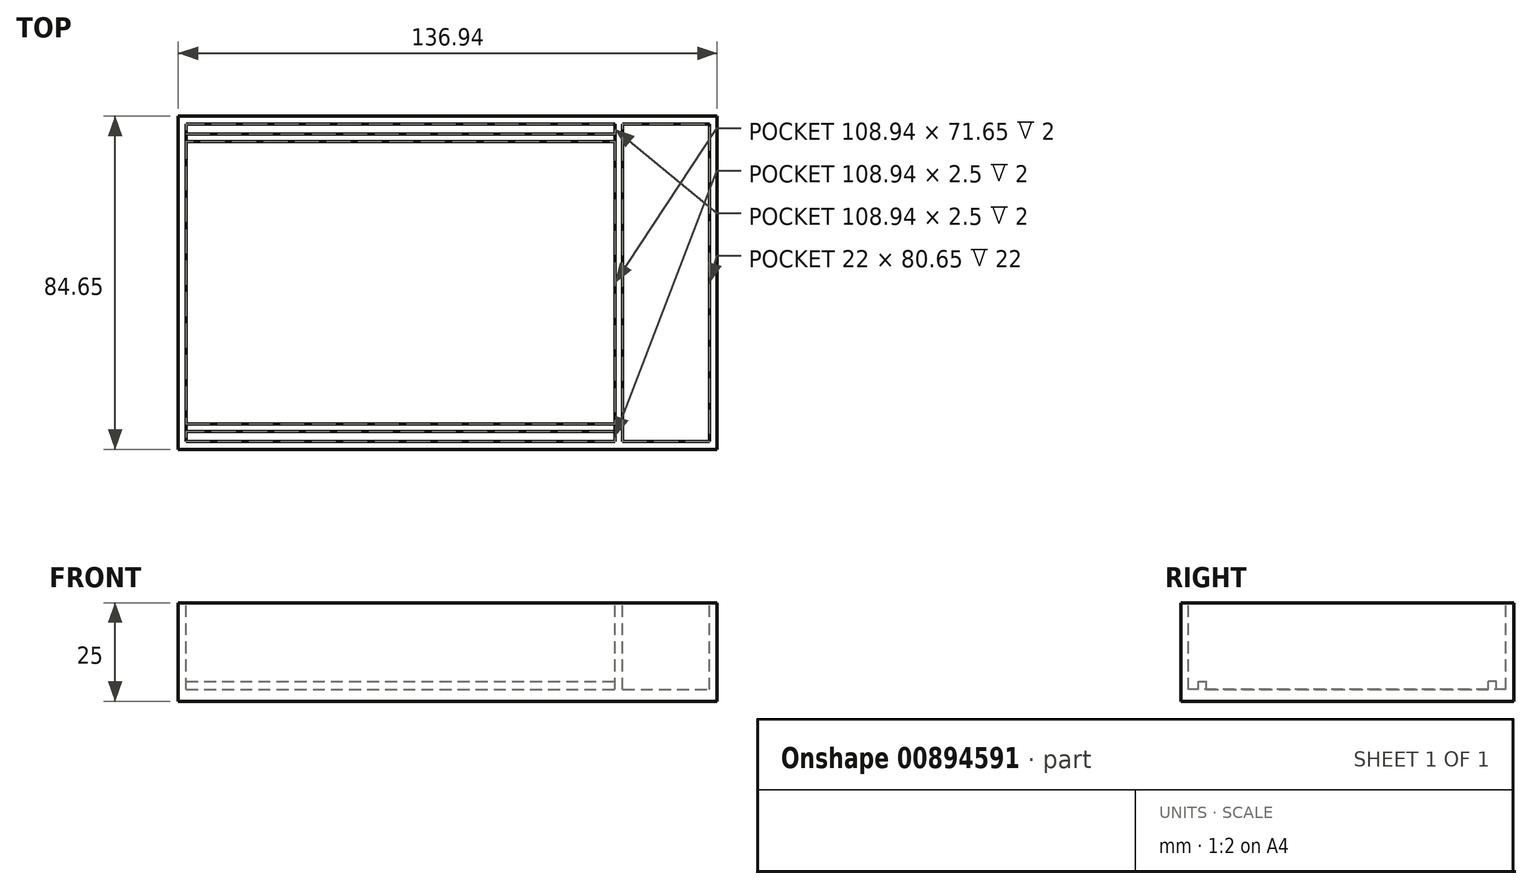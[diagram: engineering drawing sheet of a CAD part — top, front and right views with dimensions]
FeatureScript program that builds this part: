
annotation { "Feature Type Name" : "Feature", "Feature Type Description" : "" }
export const myFeature = defineFeature(function(context is Context, id is Id, definition is map)
    precondition{}
    {
        {
            var Q0;
            Q0=qCreatedBy(makeId("Top.planeOp"),FACE);
            var sketch = newSketch(context, id + "F0", { "sketchPlane" : qUnion([Q0])});
            skLineSegment(sketch, "E0.bottom", {"start": v(0, 0) * mm, "end": v(136.94, 0) * mm});
            skLineSegment(sketch, "E0.top", {"start": v(0, 84.65) * mm, "end": v(136.94, 84.65) * mm});
            skLineSegment(sketch, "E0.left", {"start": v(0, 0) * mm, "end": v(0, 84.65) * mm});
            skLineSegment(sketch, "E0.right", {"start": v(136.94, 0) * mm, "end": v(136.94, 84.65) * mm});
            skSolve(sketch);
        }
        {
            var Q0;
            Q0=makeQuery(id+"F0.imprint","IMPRINT",FACE,{"disambiguationData":[TD([[makeQuery(id+"F0.imprint","IMPRINT",EDGE,{"derivedFrom":sQuery(id+"F0.wireOp",EDGE,"E0.bottom")}),1.0]])]});
            extrude(context, id + "F1", {"entities" : qUnion([Q0]), "depth" : 25 * mm, "offsetDistance" : 25 * mm});
        }
        {
            var Q0;
            Q0=makeQuery(id+"F1.opExtrude","CAP_FACE",FACE,{"disambiguationData":[OSD([sQuery(id+"F0.wireOp",EDGE,"E0.bottom"),sQuery(id+"F0.wireOp",EDGE,"E0.top"),sQuery(id+"F0.wireOp",EDGE,"E0.left"),sQuery(id+"F0.wireOp",EDGE,"E0.right")])],"isStart":false});
            var sketch = newSketch(context, id + "F2", { "sketchPlane" : qUnion([Q0])});
            skLineSegment(sketch, "E1.bottom", {"start": v(2, 6.5) * mm, "end": v(110.94, 6.5) * mm});
            skLineSegment(sketch, "E1.top", {"start": v(2, 78.15) * mm, "end": v(110.94, 78.15) * mm});
            skLineSegment(sketch, "E1.left", {"start": v(2, 6.5) * mm, "end": v(2, 78.15) * mm});
            skLineSegment(sketch, "E1.right", {"start": v(110.94, 6.5) * mm, "end": v(110.94, 78.15) * mm});
            skLineSegment(sketch, "E2.bottom", {"start": v(2, 82.65) * mm, "end": v(110.94, 82.65) * mm});
            skLineSegment(sketch, "E2.top", {"start": v(2, 80.15) * mm, "end": v(110.94, 80.15) * mm});
            skLineSegment(sketch, "E2.left", {"start": v(2, 82.65) * mm, "end": v(2, 80.15) * mm});
            skLineSegment(sketch, "E2.right", {"start": v(110.94, 82.65) * mm, "end": v(110.94, 80.15) * mm});
            skLineSegment(sketch, "E3.bottom", {"start": v(2, 4.5) * mm, "end": v(110.94, 4.5) * mm});
            skLineSegment(sketch, "E3.top", {"start": v(2, 2) * mm, "end": v(110.94, 2) * mm});
            skLineSegment(sketch, "E3.left", {"start": v(2, 4.5) * mm, "end": v(2, 2) * mm});
            skLineSegment(sketch, "E3.right", {"start": v(110.94, 4.5) * mm, "end": v(110.94, 2) * mm});
            skSolve(sketch);
        }
        {
            var Q0;
            Q0=makeQuery(id+"F2.imprint","IMPRINT",FACE,{"disambiguationData":[TD([[makeQuery(id+"F2.imprint","IMPRINT",EDGE,{"derivedFrom":sQuery(id+"F2.wireOp",EDGE,"E1.bottom")}),1.0]])]});
            var Q1;
            Q1=makeQuery(id+"F2.imprint","IMPRINT",FACE,{"disambiguationData":[TD([[makeQuery(id+"F2.imprint","IMPRINT",EDGE,{"derivedFrom":sQuery(id+"F2.wireOp",EDGE,"E3.bottom")}),-1.0]])]});
            var Q2;
            Q2=makeQuery(id+"F2.imprint","IMPRINT",FACE,{"disambiguationData":[TD([[makeQuery(id+"F2.imprint","IMPRINT",EDGE,{"derivedFrom":sQuery(id+"F2.wireOp",EDGE,"E2.bottom")}),-1.0]])]});
            extrude(context, id + "F3", {"entities" : qUnion([Q0, Q1, Q2]), "operationType" : NewBodyOperationType.REMOVE, "oppositeDirection" : true, "depth" : 22 * mm, "offsetDistance" : 25 * mm});
        }
        {
            var Q0;
            Q0=makeQuery(id+"F1.opExtrude","CAP_FACE",FACE,{"disambiguationData":[OSD([sQuery(id+"F0.wireOp",EDGE,"E0.bottom"),sQuery(id+"F0.wireOp",EDGE,"E0.top"),sQuery(id+"F0.wireOp",EDGE,"E0.left"),sQuery(id+"F0.wireOp",EDGE,"E0.right")])],"isStart":false});
            var sketch = newSketch(context, id + "F4", { "sketchPlane" : qUnion([Q0])});
            skLineSegment(sketch, "E4.bottom", {"start": v(112.94, 82.65) * mm, "end": v(134.94, 82.65) * mm});
            skLineSegment(sketch, "E4.top", {"start": v(112.94, 2) * mm, "end": v(134.94, 2) * mm});
            skLineSegment(sketch, "E4.left", {"start": v(112.94, 82.65) * mm, "end": v(112.94, 2) * mm});
            skLineSegment(sketch, "E4.right", {"start": v(134.94, 82.65) * mm, "end": v(134.94, 2) * mm});
            skSolve(sketch);
        }
        {
            var Q0;
            Q0=makeQuery(id+"F4.imprint","IMPRINT",FACE,{"disambiguationData":[TD([[makeQuery(id+"F4.imprint","IMPRINT",EDGE,{"derivedFrom":sQuery(id+"F4.wireOp",EDGE,"E4.bottom")}),-1.0]])]});
            extrude(context, id + "F5", {"entities" : qUnion([Q0]), "operationType" : NewBodyOperationType.REMOVE, "oppositeDirection" : true, "depth" : 22 * mm, "offsetDistance" : 25 * mm});
        }
        {
            var Q0;
            Q0=makeQuery(id+"F1.opExtrude","CAP_FACE",FACE,{"disambiguationData":[OSD([sQuery(id+"F0.wireOp",EDGE,"E0.bottom"),sQuery(id+"F0.wireOp",EDGE,"E0.top"),sQuery(id+"F0.wireOp",EDGE,"E0.left"),sQuery(id+"F0.wireOp",EDGE,"E0.right")])],"isStart":false});
            var sketch = newSketch(context, id + "F6", { "sketchPlane" : qUnion([Q0])});
            skLineSegment(sketch, "E5.bottom", {"start": v(2, 80.15) * mm, "end": v(110.94, 80.15) * mm});
            skLineSegment(sketch, "E5.top", {"start": v(2, 78.15) * mm, "end": v(110.94, 78.15) * mm});
            skLineSegment(sketch, "E5.left", {"start": v(2, 80.15) * mm, "end": v(2, 78.15) * mm});
            skLineSegment(sketch, "E5.right", {"start": v(110.94, 80.15) * mm, "end": v(110.94, 78.15) * mm});
            skLineSegment(sketch, "E6.bottom", {"start": v(110.94, 4.5) * mm, "end": v(2, 4.5) * mm});
            skLineSegment(sketch, "E6.top", {"start": v(110.94, 6.5) * mm, "end": v(2, 6.5) * mm});
            skLineSegment(sketch, "E6.left", {"start": v(110.94, 4.5) * mm, "end": v(110.94, 6.5) * mm});
            skLineSegment(sketch, "E6.right", {"start": v(2, 4.5) * mm, "end": v(2, 6.5) * mm});
            skSolve(sketch);
        }
        {
            var Q0;
            Q0=makeQuery(id+"F6.imprint","IMPRINT",FACE,{"disambiguationData":[TD([[makeQuery(id+"F6.imprint","IMPRINT",EDGE,{"derivedFrom":sQuery(id+"F6.wireOp",EDGE,"E5.bottom")}),-1.0]])]});
            var Q1;
            Q1=makeQuery(id+"F6.imprint","IMPRINT",FACE,{"disambiguationData":[TD([[makeQuery(id+"F6.imprint","IMPRINT",EDGE,{"derivedFrom":sQuery(id+"F6.wireOp",EDGE,"E6.bottom")}),1.0]])]});
            extrude(context, id + "F7", {"entities" : qUnion([Q0, Q1]), "operationType" : NewBodyOperationType.REMOVE, "oppositeDirection" : true, "depth" : 20 * mm, "offsetDistance" : 25 * mm});
        }
    });
